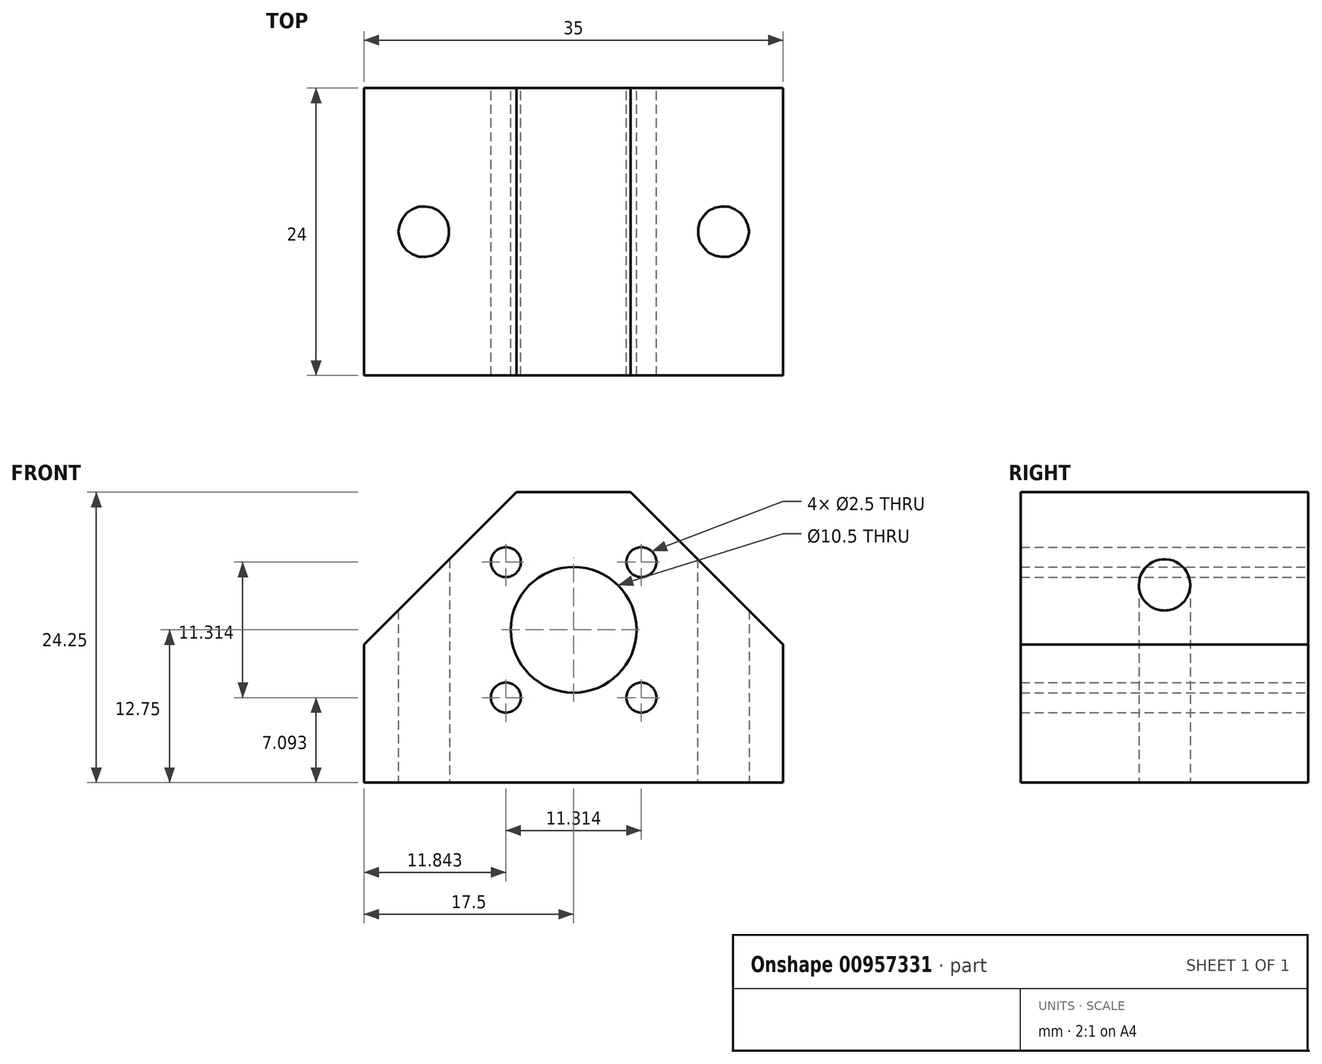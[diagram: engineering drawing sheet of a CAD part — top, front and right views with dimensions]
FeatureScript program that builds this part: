
annotation { "Feature Type Name" : "Feature", "Feature Type Description" : "" }
export const myFeature = defineFeature(function(context is Context, id is Id, definition is map)
    precondition{}
    {
        {
            var Q0;
            Q0=qCreatedBy(makeId("Top.planeOp"),FACE);
            var sketch = newSketch(context, id + "F0", { "sketchPlane" : qUnion([Q0])});
            skLineSegment(sketch, "E0.bottom", {"start": v(-17.5, 12) * mm, "end": v(17.5, 12) * mm});
            skLineSegment(sketch, "E0.top", {"start": v(-17.5, -12) * mm, "end": v(17.5, -12) * mm});
            skLineSegment(sketch, "E0.left", {"start": v(-17.5, 12) * mm, "end": v(-17.5, -12) * mm});
            skLineSegment(sketch, "E0.right", {"start": v(17.5, 12) * mm, "end": v(17.5, -12) * mm});
            skPoint(sketch, "E0.middle", {"position": v(0, 0) * mm});
            skLineSegment(sketch, "E1.bottom", {"start": v(-12.5, 0) * mm, "end": v(12.5, 0) * mm, "construction": true});
            skLineSegment(sketch, "E1.top", {"start": v(-12.5, 0) * mm, "end": v(12.5, 0) * mm, "construction": true});
            skLineSegment(sketch, "E1.left", {"start": v(-12.5, 0) * mm, "end": v(-12.5, 0) * mm});
            skLineSegment(sketch, "E1.right", {"start": v(12.5, 0) * mm, "end": v(12.5, 0) * mm});
            skCircle(sketch, "E2", {"center": v(-12.5, 0) * mm, "radius": 2.15 * mm, "construction": true});
            skCircle(sketch, "E3", {"center": v(12.5, 0) * mm, "radius": 2.15 * mm});
            skCircle(sketch, "E4", {"center": v(12.5, 0) * mm, "radius": 2.15 * mm, "construction": true});
            skCircle(sketch, "E5", {"center": v(-12.5, 0) * mm, "radius": 2.15 * mm});
            skSolve(sketch);
        }
        {
            var Q0;
            Q0=qSketchRegion(id+"F0",true);
            extrude(context, id + "F1", {"entities" : qUnion([Q0]), "depth" : 35 * mm, "offsetDistance" : 25 * mm});
        }
        {
            var Q0;
            Q0=qCreatedBy(makeId("Front.planeOp"),FACE);
            var sketch = newSketch(context, id + "F2", { "sketchPlane" : qUnion([Q0])});
            skLineSegment(sketch, "E6", {"start": v(0, 0) * mm, "end": v(0, 12.75) * mm, "construction": true});
            skArc(sketch, "E7", {"start": v(11.5, 12.75) * mm, "mid": v(0, 24.25) * mm, "end": v(-11.5, 12.75) * mm});
            skLineSegment(sketch, "E8", {"start": v(-11.5, 12.75) * mm, "end": v(-11.5, 0) * mm});
            skLineSegment(sketch, "E9.MirrorCS", {"start": v(11.5, 12.75) * mm, "end": v(11.5, 0) * mm});
            skCircle(sketch, "E10", {"center": v(0, 12.75) * mm, "radius": 5.25 * mm});
            skCircle(sketch, "E11", {"center": v(0, 12.75) * mm, "radius": 8 * mm, "construction": true});
            skLineSegment(sketch, "E12", {"start": v(0, 20.75) * mm, "end": v(0, 4.75) * mm, "construction": true});
            skPoint(sketch, "E12.startSnap0", {"position": v(0, 24.25) * mm});
            skLineSegment(sketch, "E13", {"start": v(-8, 12.75) * mm, "end": v(8, 12.75) * mm, "construction": true});
            skLineSegment(sketch, "E14", {"start": v(0, 12.75) * mm, "end": v(-5.66, 18.4) * mm, "construction": true});
            skLineSegment(sketch, "E15", {"start": v(0, 12.75) * mm, "end": v(-5.66, 7.1) * mm, "construction": true});
            skLineSegment(sketch, "E16.MirrorCS", {"start": v(0, 12.75) * mm, "end": v(5.66, 18.4) * mm, "construction": true});
            skLineSegment(sketch, "E17.MirrorCS", {"start": v(0, 12.75) * mm, "end": v(5.66, 7.1) * mm, "construction": true});
            skCircle(sketch, "E18", {"center": v(-5.66, 18.4) * mm, "radius": 1.25 * mm});
            skCircle(sketch, "E19", {"center": v(-5.66, 7.1) * mm, "radius": 1.25 * mm});
            skCircle(sketch, "E20", {"center": v(5.66, 7.1) * mm, "radius": 1.25 * mm});
            skCircle(sketch, "E21", {"center": v(5.66, 18.4) * mm, "radius": 1.25 * mm});
            skLineSegment(sketch, "E22", {"start": v(-11.5, 0) * mm, "end": v(11.5, 0) * mm});
            skLineSegment(sketch, "E23", {"start": v(-17.5, 11.51) * mm, "end": v(-4.76, 24.25) * mm});
            skLineSegment(sketch, "E24", {"start": v(0, 24.25) * mm, "end": v(-4.76, 24.25) * mm});
            skLineSegment(sketch, "E25", {"start": v(-17.5, 35) * mm, "end": v(-17.5, 11.51) * mm});
            skLineSegment(sketch, "E26", {"start": v(-17.5, 35) * mm, "end": v(0, 35) * mm});
            skLineSegment(sketch, "E27.MirrorCS", {"start": v(17.5, 35) * mm, "end": v(0, 35) * mm});
            skLineSegment(sketch, "E28.MirrorCS", {"start": v(17.5, 35) * mm, "end": v(17.5, 11.51) * mm});
            skLineSegment(sketch, "E29.MirrorCS", {"start": v(0, 24.25) * mm, "end": v(4.76, 24.25) * mm});
            skLineSegment(sketch, "E30.MirrorCS", {"start": v(17.5, 11.51) * mm, "end": v(4.76, 24.25) * mm});
            skLineSegment(sketch, "E31", {"start": v(-17.5, 11.51) * mm, "end": v(-17.5, 0) * mm});
            skLineSegment(sketch, "E32", {"start": v(-17.5, 0) * mm, "end": v(-11.5, 0) * mm});
            skLineSegment(sketch, "E33", {"start": v(17.5, 11.51) * mm, "end": v(17.5, 0) * mm});
            skLineSegment(sketch, "E34", {"start": v(17.5, 0) * mm, "end": v(11.5, 0) * mm});
            skSolve(sketch);
        }
        {
            var Q0;
            {var subQ0=sQuery(id+"F2.wireOp",EDGE,"E29.MirrorCS");Q0=makeQuery(id+"F2.imprint","IMPRINT",FACE,{"disambiguationData":[TD([[makeQuery(id+"F2.imprint","IMPRINT",EDGE,{"derivedFrom":subQ0}),-1.0]])]});}
            var Q1;
            {var subQ0=sQuery(id+"F2.wireOp",EDGE,"E24");Q1=makeQuery(id+"F2.imprint","IMPRINT",FACE,{"disambiguationData":[TD([[makeQuery(id+"F2.imprint","IMPRINT",EDGE,{"derivedFrom":subQ0}),1.0]])]});}
            var Q2;
            {var subQ1=sQuery(id+"F2.wireOp",EDGE,"E8");Q2=makeQuery(id+"F2.imprint","IMPRINT",FACE,{"disambiguationData":[TD([[makeQuery(id+"F2.imprint","IMPRINT",EDGE,{"derivedFrom":subQ1}),1.0]])]});}
            var Q3;
            {var subQ4=sQuery(id+"F2.wireOp",EDGE,"E8");Q3=makeQuery(id+"F2.imprint","IMPRINT",FACE,{"disambiguationData":[TD([[makeQuery(id+"F2.imprint","IMPRINT",EDGE,{"derivedFrom":subQ4}),-1.0]])]});}
            var Q4;
            {var subQ4=sQuery(id+"F2.wireOp",EDGE,"E9.MirrorCS");Q4=makeQuery(id+"F2.imprint","IMPRINT",FACE,{"disambiguationData":[TD([[makeQuery(id+"F2.imprint","IMPRINT",EDGE,{"derivedFrom":subQ4}),1.0]])]});}
            extrude(context, id + "F3", {"entities" : qUnion([Q0, Q1, Q2, Q3, Q4]), "operationType" : NewBodyOperationType.INTERSECT, "endBound" : BoundingType.SYMMETRIC, "depth" : 24 * mm, "offsetDistance" : 25 * mm});
        }
    });
